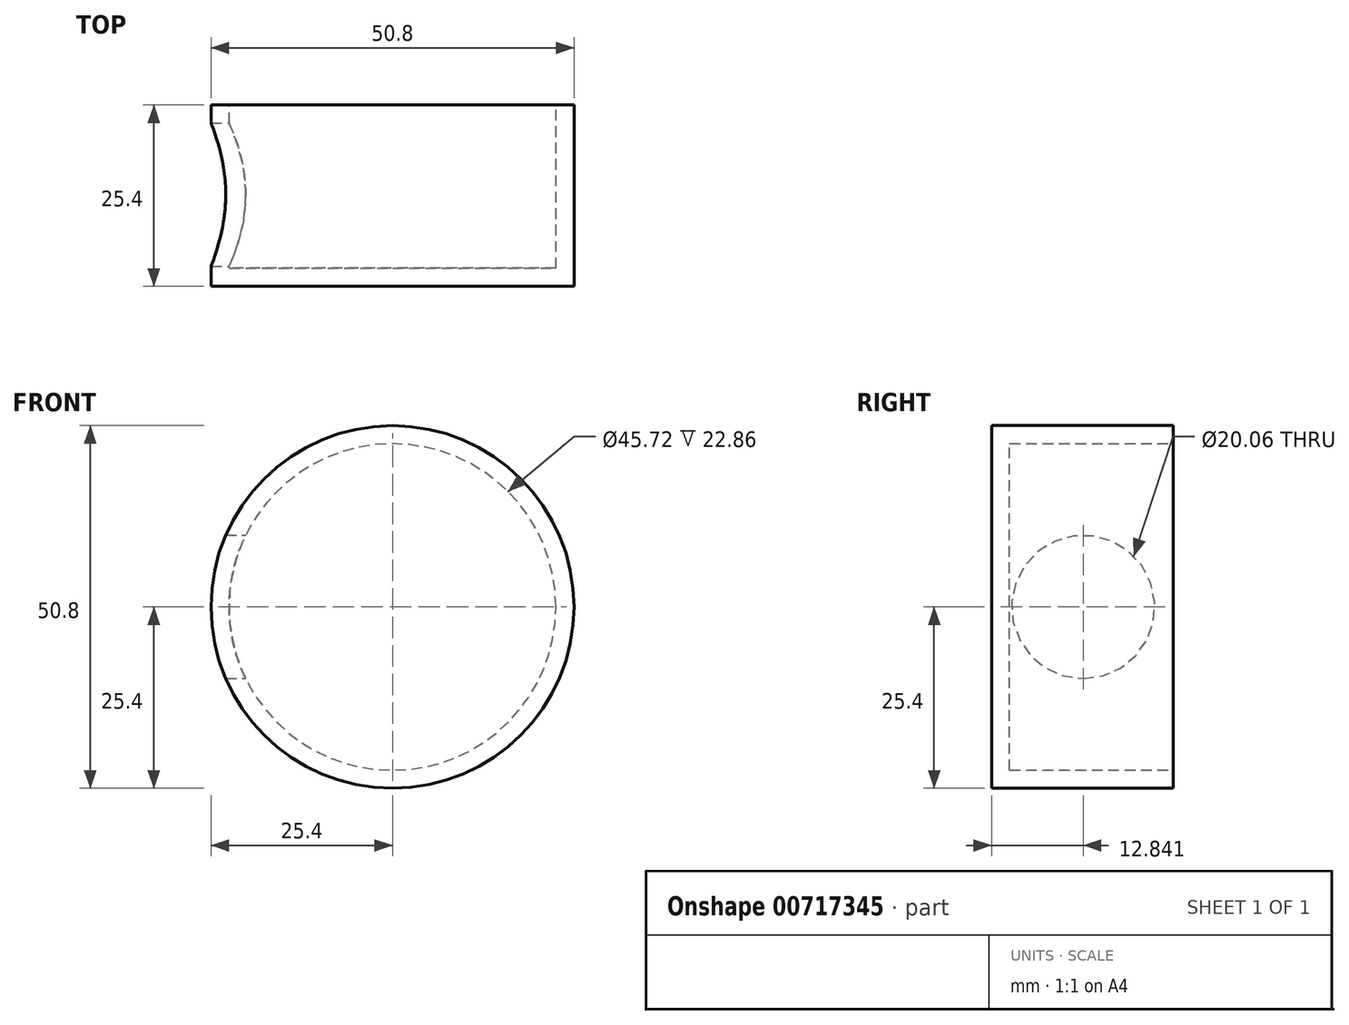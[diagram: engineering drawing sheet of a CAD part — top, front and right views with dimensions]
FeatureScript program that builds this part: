
annotation { "Feature Type Name" : "Feature", "Feature Type Description" : "" }
export const myFeature = defineFeature(function(context is Context, id is Id, definition is map)
    precondition{}
    {
        {
            var Q0;
            Q0=qCreatedBy(makeId("Front.planeOp"),FACE);
            var sketch = newSketch(context, id + "F0", { "sketchPlane" : qUnion([Q0])});
            skCircle(sketch, "E0", {"center": v(0, 0) * mm, "radius": 25.4 * mm});
            skSolve(sketch);
        }
        {
            var Q0;
            Q0=makeQuery(id+"F0.imprint","IMPRINT",FACE,{"disambiguationData":[TD([[makeQuery(id+"F0.imprint","IMPRINT",EDGE,{"derivedFrom":sQuery(id+"F0.wireOp",EDGE,"E0")}),1.0]])]});
            extrude(context, id + "F1", {"entities" : qUnion([Q0]), "depth" : 25.4 * mm, "offsetDistance" : 25.4 * mm});
        }
        {
            var Q0;
            Q0=makeQuery(id+"F1.opExtrude","CAP_FACE",FACE,{"disambiguationData":[OSD([sQuery(id+"F0.wireOp",EDGE,"E0")])],"isStart":true});
            shell(context, id + "F2", {"entities" : qUnion([Q0]), "thickness" : 2.54 * mm});
        }
        {
            var Q0;
            Q0=qCreatedBy(makeId("Right.planeOp"),FACE);
            var sketch = newSketch(context, id + "F3", { "sketchPlane" : qUnion([Q0])});
            skCircle(sketch, "E1", {"center": v(-12.56, 0) * mm, "radius": 10.03 * mm});
            skSolve(sketch);
        }
        {
            var Q0;
            Q0 = qSketchRegion(id + "F3", true);
            extrude(context, id + "F4", {"entities" : qUnion([Q0]), "operationType" : NewBodyOperationType.REMOVE, "endBound" : BoundingType.THROUGH_ALL, "oppositeDirection" : true, "depth" : 25.4 * mm, "offsetDistance" : 25.4 * mm});
        }
    });
